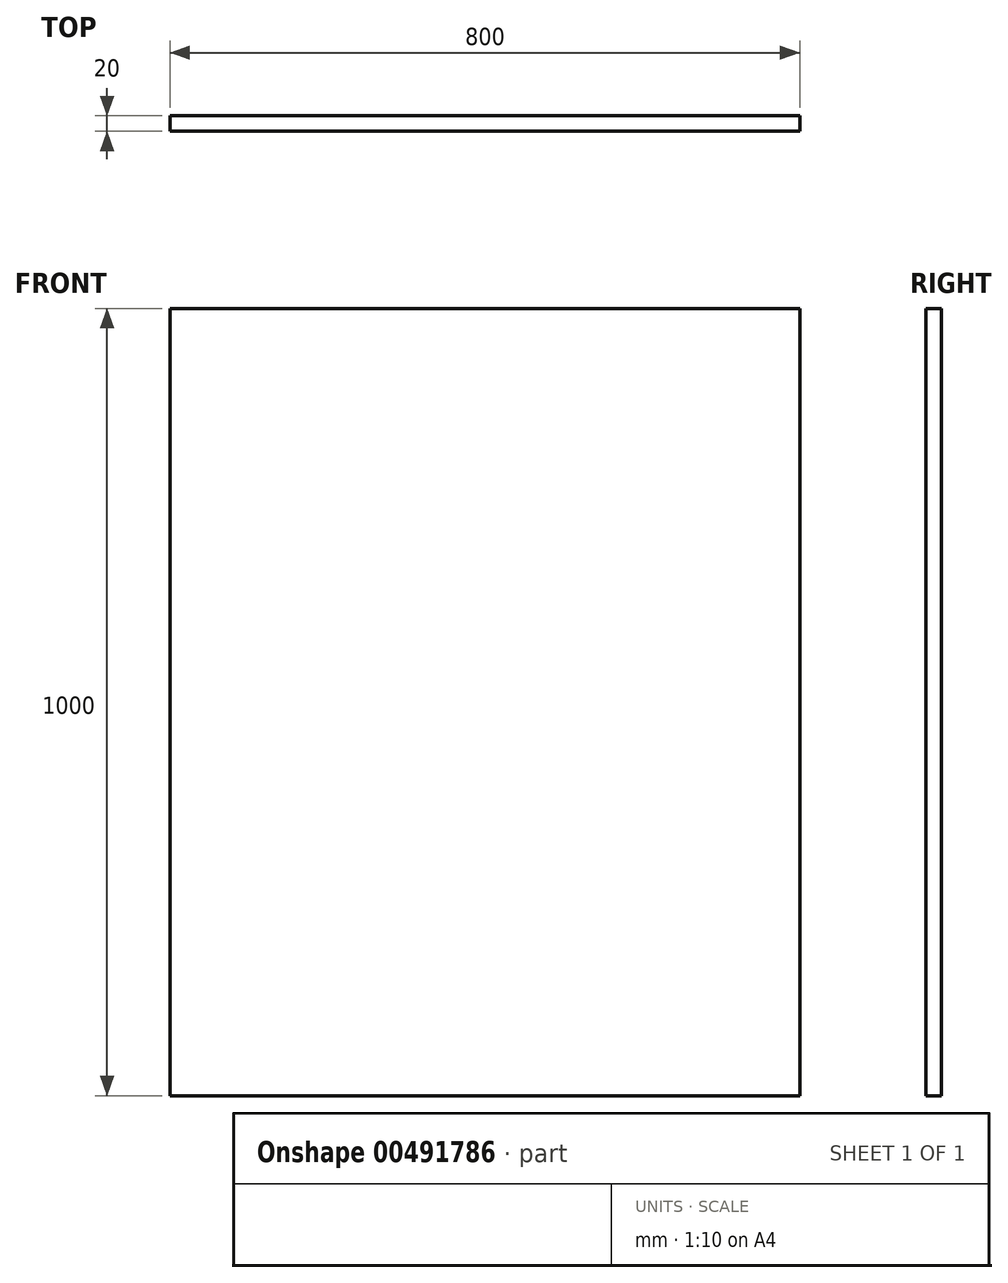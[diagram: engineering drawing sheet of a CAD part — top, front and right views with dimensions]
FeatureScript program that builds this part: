
annotation { "Feature Type Name" : "Feature", "Feature Type Description" : "" }
export const myFeature = defineFeature(function(context is Context, id is Id, definition is map)
    precondition{}
    {
        {
            var Q0;
            Q0=qCreatedBy(makeId("Front.planeOp"),FACE);
            var sketch = newSketch(context, id + "F0", { "sketchPlane" : qUnion([Q0])});
            skLineSegment(sketch, "E0.bottom", {"start": v(0, 0) * mm, "end": v(800, 0) * mm});
            skLineSegment(sketch, "E0.top", {"start": v(0, 1000) * mm, "end": v(800, 1000) * mm});
            skLineSegment(sketch, "E0.left", {"start": v(0, 0) * mm, "end": v(0, 1000) * mm});
            skLineSegment(sketch, "E0.right", {"start": v(800, 0) * mm, "end": v(800, 1000) * mm});
            skSolve(sketch);
        }
        {
            var Q0;
            Q0=makeQuery(id+"F0.imprint","IMPRINT",FACE,{"disambiguationData":[TD([[makeQuery(id+"F0.imprint","IMPRINT",EDGE,{"derivedFrom":sQuery(id+"F0.wireOp",EDGE,"E0.bottom")}),1.0]])]});
            extrude(context, id + "F1", {"entities" : qUnion([Q0]), "depth" : 20 * mm, "offsetDistance" : 25 * mm});
        }
    });
